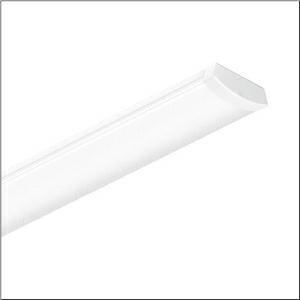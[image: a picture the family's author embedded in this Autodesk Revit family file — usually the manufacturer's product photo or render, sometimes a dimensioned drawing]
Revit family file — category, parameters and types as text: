
# Revit family: siluette_r__21_51ln12mkm40a_b89c
name_source: partatom
category: Lighting Fixtures
units: mm (PartAtom-declared; Revit-internal decimal feet)

## family parameters
Cut with Voids When Loaded = No
Host = Face
Light Source = No
Part Type = Normal
Room Calculation Point = No
Round Connector Dimension = Use Diameter
Shared = No

## types (1)
- --- (1 x LED, 2980 lm, 20.6 W, 5000K)
    Apparent Load = 21 VA
    CIE Flux Codes = 43 73 92 94 100
    Color Rendering = 80
    Color Temperature = 5000K
    Default Elevation = 1800 mm
    Description = Siluette® 21, office luminaire, primary optical cover: enclosure, of PC, frosted, light emission: direct distribution, primary light characteristic: symmetric, installation type: suspended mounting, surface-mounted, LED, rated luminous flux: 5.010lm, luminous efficacy: 144lm/W, light colour: 830/840/850, colour temperature: 3000/4000/5000K, control gear: ON/OFF Multilumen, with terminal, 3-pole, mains connection: 220..240V, AC, 50/60Hz, rated input power: 35W, housing, of sheet steel, white, length: 1.200mm, width: 152mm, height: 53mm, end cap, of PMMA, white, protection rating (complete): IP44, insulation class (complete): insulation class I (protective earthing), certification: CE, UKCA, protection symbol: D, impact resistance: IK04, permissible operating ambient temperature: -20..+40°C, contact your sales advisor before using the luminaires in applications with unclear chemical exposure, large temperature fluctuations or condensation-forming humidity, corresponds to IFS (International Featured Standards) requirements for safety and quality in the food industry, packaging unit: 1 piece
    Height = 52 mm  [stored 0.170604 ft]
    Lamp = 1 x LED
    Lamp Light Flux = 2980 lm
    Lamp Power = 20.6 W
    Lamp count = 1
    Length = 1185 mm
    Luminous efficacy = 145 lm/W
    Manufacturer = Siteco
    ModVariant = No
    Model = 51LN12MKM40A
    Mounting Place = Ceiling
    Mounting Type = Pendant
    Number of Poles = 1
    OnlyDefault = Yes
    Power Factor = 1
    Product Name = Siluette® 21
    Product group = office luminaire | ceiling pendant
    ProductGroupID = 903
    Protection Class = Protection class I
    Protection Degree = IP 44
    RLX_Detail_Level = 1
    RLX_Emergency_Light_Flux = 0 lm
    RLX_Emergency_Type = 0
    RLX_Emergency_Type_DB = No
    RlxData = <blob elided: 19249 chars, md5=74f4cfc8>
    Socket = socket
    Standby Power = 0 W
    System Light Flux = 2980 lm
    System Power = 21 W
    Type Comments = individual setting: colour temperature 5000K, luminous flux: 60 % | (OFF | OFF | ON) | 200 mA
    Type Image = l_1296910.jpg
    URL = http://relux.com
    VarID = @adj_079553
    Voltage = 0 V
    Weight = 0.00 kg
    Width = 152 mm

note: [stored X ft] marks values corroborated as IEEE doubles in the binary element streams (Revit-internal decimal feet)

## geometry (parser evidence)
native form markers: Blend x4, Sweep x13
no freeform markers — native parametric forms only
